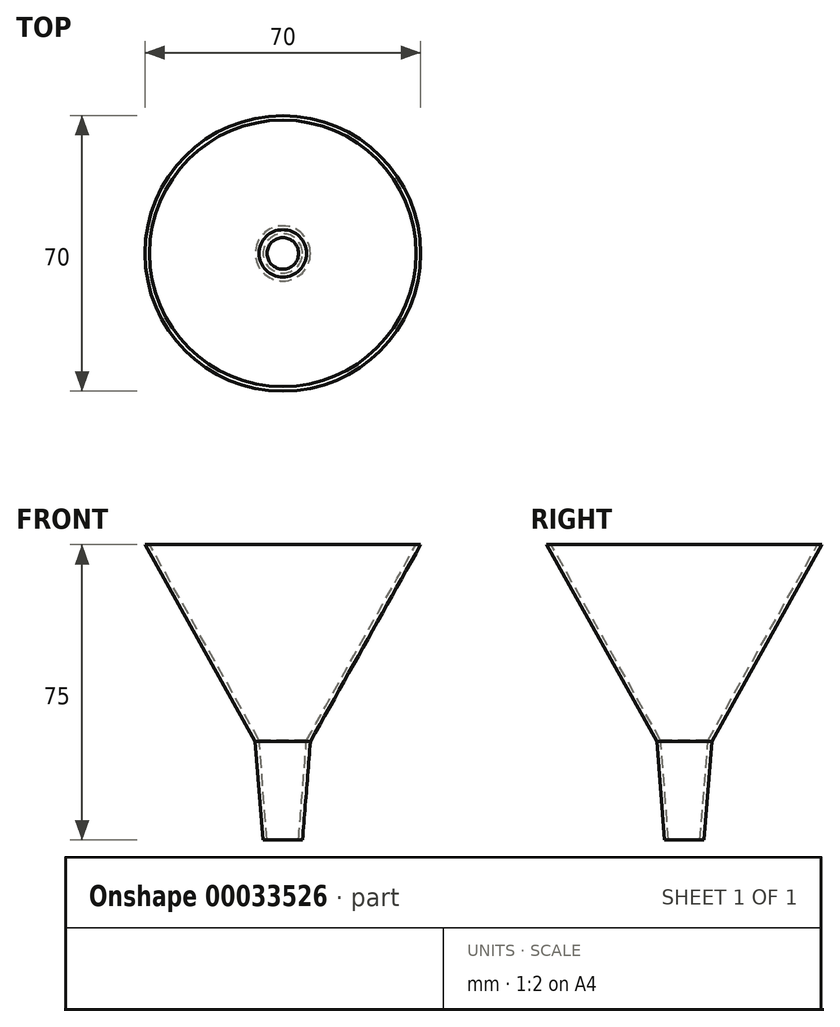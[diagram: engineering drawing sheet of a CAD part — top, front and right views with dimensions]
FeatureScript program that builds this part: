
annotation { "Feature Type Name" : "Feature", "Feature Type Description" : "" }
export const myFeature = defineFeature(function(context is Context, id is Id, definition is map)
    precondition{}
    {
        {
            var Q0;
            Q0=qCreatedBy(makeId("Front.planeOp"),FACE);
            var sketch = newSketch(context, id + "F0", { "sketchPlane" : qUnion([Q0])});
            skLineSegment(sketch, "E0", {"start": v(0, -25) * mm, "end": v(5, -25) * mm});
            skLineSegment(sketch, "E1", {"start": v(5, -25) * mm, "end": v(7, 0) * mm});
            skLineSegment(sketch, "E2", {"start": v(7, 0) * mm, "end": v(35, 50) * mm});
            skLineSegment(sketch, "E3", {"start": v(35, 50) * mm, "end": v(0, 50) * mm});
            skLineSegment(sketch, "E4", {"start": v(0, 50) * mm, "end": v(0, -25) * mm});
            skSolve(sketch);
        }
        {
            var Q0;
            Q0 = qSketchRegion(id + "F0", true);
            var Q1;
            Q1=sQuery(id+"F0.wireOp",EDGE,"E4");
            revolve(context, id + "F1", {"entities" : qUnion([Q0]), "axis" : qUnion([Q1]), "revolveType" : RevolveType.FULL});
        }
        {
            var Q0;
            Q0=makeQuery(id+"F1.opRevolve","SWEPT_FACE",FACE,{"disambiguationData":[OSD([sQuery(id+"F0.wireOp",EDGE,"E3")])]});
            var Q1;
            Q1=makeQuery(id+"F1.opRevolve","SWEPT_FACE",FACE,{"disambiguationData":[OSD([sQuery(id+"F0.wireOp",EDGE,"E0")])]});
            shell(context, id + "F2", {"entities" : qUnion([Q0, Q1]), "thickness" : 1 * mm});
        }
    });
